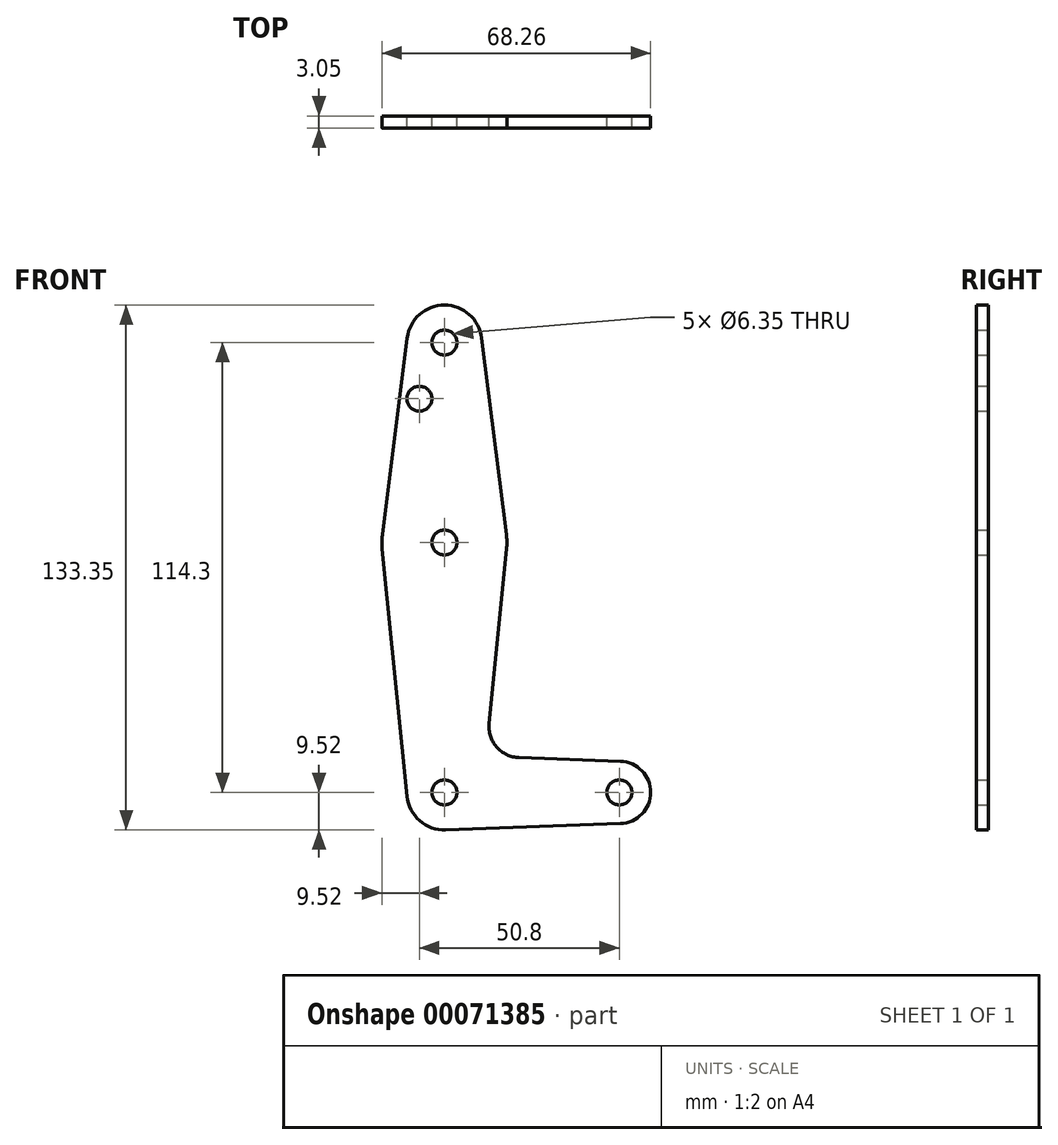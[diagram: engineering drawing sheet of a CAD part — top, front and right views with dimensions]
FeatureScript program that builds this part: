
annotation { "Feature Type Name" : "Feature", "Feature Type Description" : "" }
export const myFeature = defineFeature(function(context is Context, id is Id, definition is map)
    precondition{}
    {
        {
            var Q0;
            Q0=qCreatedBy(makeId("Front.planeOp"),FACE);
            var sketch = newSketch(context, id + "F0", { "sketchPlane" : qUnion([Q0])});
            skLineSegment(sketch, "E0", {"start": v(0, 114.3) * mm, "end": v(0, 63.5) * mm});
            skLineSegment(sketch, "E1", {"start": v(0, 63.5) * mm, "end": v(0, 0) * mm, "construction": true});
            skLineSegment(sketch, "E2", {"start": v(0, 0) * mm, "end": v(44.45, 0) * mm, "construction": true});
            skCircle(sketch, "E3", {"center": v(0, 114.3) * mm, "radius": 9.53 * mm});
            skCircle(sketch, "E4", {"center": v(0, 63.5) * mm, "radius": 15.88 * mm});
            skCircle(sketch, "E5", {"center": v(44.45, 0) * mm, "radius": 7.94 * mm});
            skLineSegment(sketch, "E6", {"start": v(-9.45, 115.5) * mm, "end": v(-15.75, 65.48) * mm});
            skLineSegment(sketch, "E7", {"start": v(9.45, 115.5) * mm, "end": v(15.8, 65.13) * mm});
            skLineSegment(sketch, "E8", {"start": v(0, -9.53) * mm, "end": v(44.73, -7.93) * mm});
            skCircle(sketch, "E9", {"center": v(0, 114.3) * mm, "radius": 3.18 * mm});
            skCircle(sketch, "E10", {"center": v(0, 63.5) * mm, "radius": 3.18 * mm});
            skCircle(sketch, "E11", {"center": v(0, 0) * mm, "radius": 3.18 * mm});
            skCircle(sketch, "E12", {"center": v(44.45, 0) * mm, "radius": 3.18 * mm});
            skCircle(sketch, "E13", {"center": v(-6.35, 100.03) * mm, "radius": 3.18 * mm});
            skLineSegment(sketch, "E14", {"start": v(-15.8, 61.91) * mm, "end": v(-9.48, -0.95) * mm});
            skCircle(sketch, "E15", {"center": v(0, 0) * mm, "radius": 9.53 * mm});
            skLineSegment(sketch, "E16", {"start": v(15.8, 61.91) * mm, "end": v(11.34, 17.59) * mm});
            skLineSegment(sketch, "E17", {"start": v(18.97, 8.85) * mm, "end": v(44.73, 7.93) * mm});
            skArc(sketch, "E18.filletArc", {"start": v(11.34, 17.59) * mm, "mid": v(13.26, 11.57) * mm, "end": v(18.97, 8.85) * mm});
            skSolve(sketch);
        }
        {
            var Q0;
            Q0 = qSketchRegion(id + "F0", true);
            extrude(context, id + "F1", {"entities" : qUnion([Q0]), "depth" : 3.05 * mm});
        }
    });
